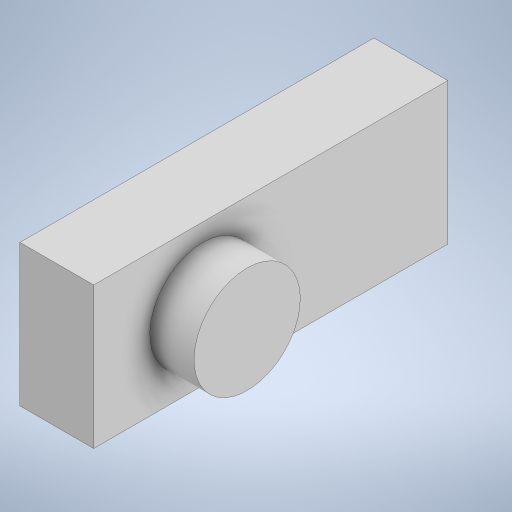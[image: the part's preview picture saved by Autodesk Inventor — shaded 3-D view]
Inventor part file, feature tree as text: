
AUTODESK INVENTOR PART (.ipt)
format: ipt  version: 2024.1 (Build 281209000, 209)  size: 256,000 bytes
history: native  units: mm
features: extrude x2, other x1, sketch x1
ambient origin geometry x8: Origin, YZ Plane, XZ Plane, XY Plane, X Axis, Y Axis, Z Axis, Center Point
bodies: Body1 (feature_tree)
feature tree (4):
  other  "Sólido1"
  sketch  "Boceto1"  dims[d0=60.0mm d1=24.0mm d2=18.0mm d3=18.5mm d4=20.0mm d5=0.0mm d6=12.5mm d7=0.0mm]
  extrude  "Extrusión1"  Depth=24.0mm
  extrude  "Extrusión2"  Depth=12.5mm
